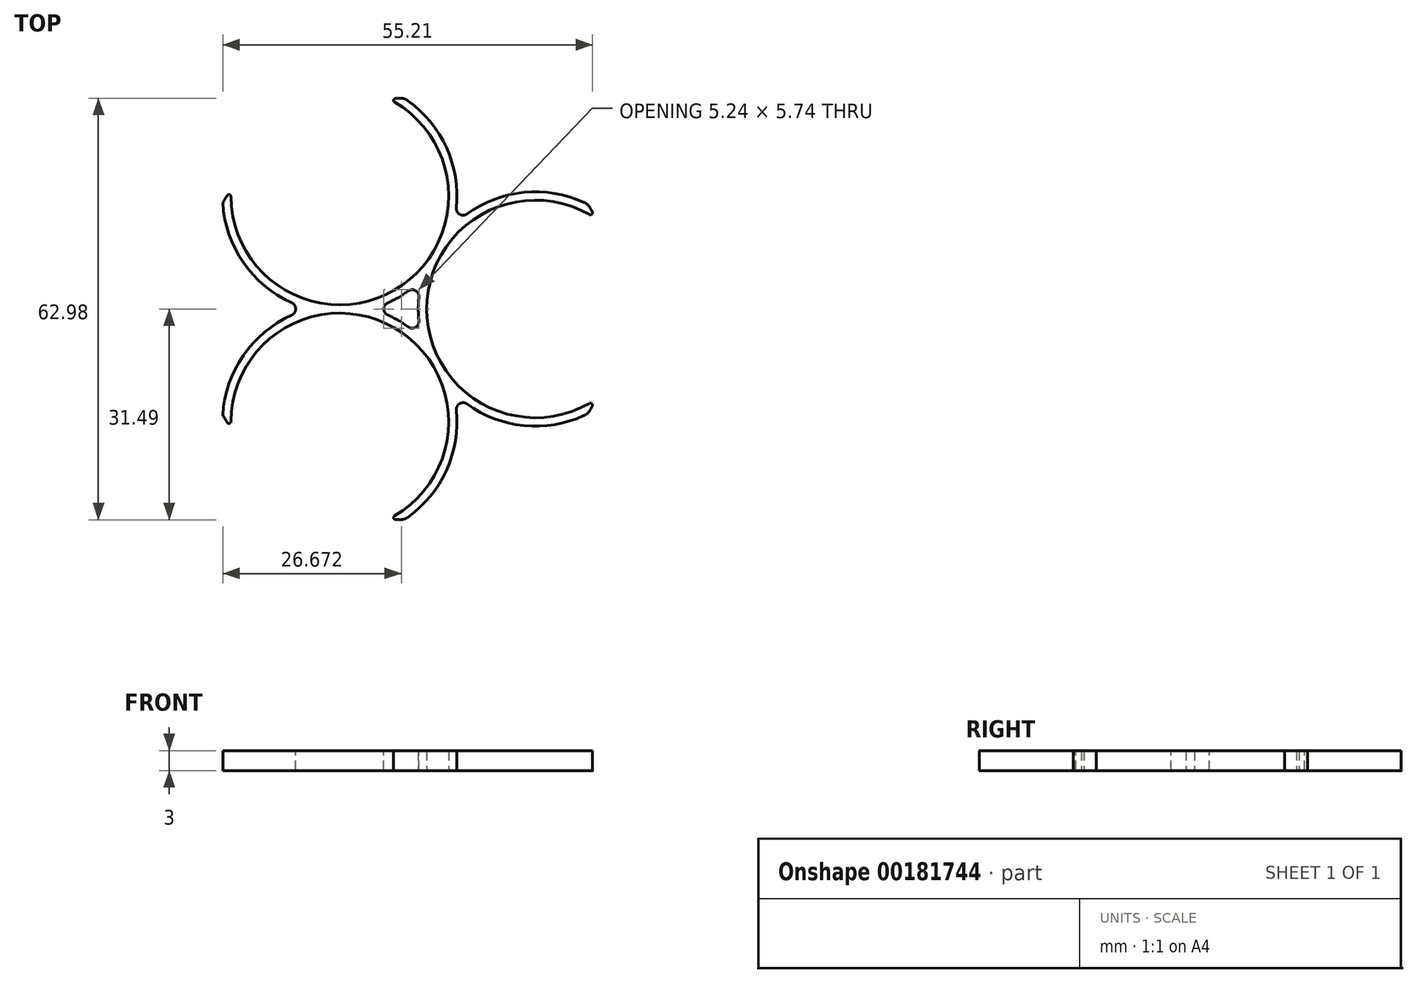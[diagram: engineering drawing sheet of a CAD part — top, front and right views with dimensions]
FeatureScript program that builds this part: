
annotation { "Feature Type Name" : "Feature", "Feature Type Description" : "" }
export const myFeature = defineFeature(function(context is Context, id is Id, definition is map)
    precondition{}
    {
        {
            var Q0;
            Q0=qCreatedBy(makeId("Top.planeOp"),FACE);
            var sketch = newSketch(context, id + "F0", { "sketchPlane" : qUnion([Q0])});
            skArc(sketch, "E0", {"start": v(-12.3, -12.45) * mm, "mid": v(-2.73, -17.29) * mm, "end": v(7.86, -15.64) * mm});
            skArc(sketch, "E1", {"start": v(8.94, 13.57) * mm, "mid": v(-16.25, 0) * mm, "end": v(8.94, -13.57) * mm});
            skArc(sketch, "E2.1.0", {"start": v(-46.7, 15.86) * mm, "mid": v(-42.83, 5.87) * mm, "end": v(-33.86, 0) * mm});
            skArc(sketch, "E2.1.1", {"start": v(-45.45, 17.84) * mm, "mid": v(-21.1, 2.8) * mm, "end": v(-21.95, 31.4) * mm});
            skArc(sketch, "E2.2.0", {"start": v(-19.62, -31.5) * mm, "mid": v(-12.9, -23.15) * mm, "end": v(-12.3, -12.45) * mm});
            skArc(sketch, "E2.2.1", {"start": v(-21.95, -31.4) * mm, "mid": v(-21.1, -2.8) * mm, "end": v(-45.45, -17.84) * mm});
            skPoint(sketch, "E2.center", {"position": v(-19.49, 0) * mm});
            skArc(sketch, "E3", {"start": v(-45.45, 17.84) * mm, "mid": v(-46.1, 16.86) * mm, "end": v(-46.7, 15.86) * mm});
            skArc(sketch, "E4.trimOffspring", {"start": v(-46.7, -15.86) * mm, "mid": v(-46.1, -16.86) * mm, "end": v(-45.45, -17.84) * mm});
            skArc(sketch, "E5.trimOffspring", {"start": v(-21.95, -31.4) * mm, "mid": v(-20.78, -31.47) * mm, "end": v(-19.62, -31.5) * mm});
            skArc(sketch, "E6.trimOffspring", {"start": v(7.86, -15.64) * mm, "mid": v(8.42, -14.61) * mm, "end": v(8.94, -13.57) * mm});
            skArc(sketch, "E7.trimOffspring", {"start": v(-16.93, -4.42) * mm, "mid": v(-20.48, -1.72) * mm, "end": v(-24.6, 0) * mm});
            skArc(sketch, "E8.trimOffspring", {"start": v(-12.3, 12.45) * mm, "mid": v(-12.9, 23.15) * mm, "end": v(-19.62, 31.5) * mm});
            skArc(sketch, "E9.trimOffspring", {"start": v(-16.93, 4.42) * mm, "mid": v(-17.5, 0) * mm, "end": v(-16.93, -4.42) * mm});
            skArc(sketch, "E10.trimOffspring", {"start": v(-33.86, 0) * mm, "mid": v(-42.83, -5.87) * mm, "end": v(-46.7, -15.86) * mm});
            skArc(sketch, "E11.trimOffspring", {"start": v(-24.6, 0) * mm, "mid": v(-20.48, 1.72) * mm, "end": v(-16.93, 4.42) * mm});
            skArc(sketch, "E12.trimOffspring", {"start": v(7.86, 15.64) * mm, "mid": v(-2.73, 17.29) * mm, "end": v(-12.3, 12.45) * mm});
            skArc(sketch, "E13.trimOffspring", {"start": v(8.94, 13.57) * mm, "mid": v(8.42, 14.61) * mm, "end": v(7.86, 15.64) * mm});
            skArc(sketch, "E14.trimOffspring", {"start": v(-19.62, 31.5) * mm, "mid": v(-20.78, 31.47) * mm, "end": v(-21.95, 31.4) * mm});
            skSolve(sketch);
        }
        {
            var Q0;
            Q0=makeQuery(id+"F0.imprint","IMPRINT",FACE,{"disambiguationData":[TD([[makeQuery(id+"F0.imprint","IMPRINT",EDGE,{"derivedFrom":sQuery(id+"F0.wireOp",EDGE,"E0")}),1.0]])]});
            extrude(context, id + "F1", {"entities" : qUnion([Q0]), "depth" : 3 * mm});
        }
        {
            var Q0;
            Q0=makeQuery(id+"F1.opExtrude","SWEPT_EDGE",EDGE,{"disambiguationData":[OSD([sQuery(id+"F0.wireOp",EDGE,"E2.1.0"),sQuery(id+"F0.wireOp",EDGE,"E10.trimOffspring")])]});
            var Q1;
            Q1=makeQuery(id+"F1.opExtrude","SWEPT_EDGE",EDGE,{"disambiguationData":[OSD([sQuery(id+"F0.wireOp",EDGE,"E8.trimOffspring"),sQuery(id+"F0.wireOp",EDGE,"E12.trimOffspring")])]});
            var Q2;
            Q2=makeQuery(id+"F1.opExtrude","SWEPT_EDGE",EDGE,{"disambiguationData":[OSD([sQuery(id+"F0.wireOp",EDGE,"E0"),sQuery(id+"F0.wireOp",EDGE,"E2.2.0")])]});
            fillet(context, id + "F2", {"entities" : qUnion([Q0, Q1, Q2]), "radius" : 1 * mm, "tangentPropagation" : true, "allowEdgeOverflow" : false});
        }
        {
            var Q0;
            Q0=makeQuery(id+"F1.opExtrude","SWEPT_EDGE",EDGE,{"disambiguationData":[OSD([sQuery(id+"F0.wireOp",EDGE,"E9.trimOffspring"),sQuery(id+"F0.wireOp",EDGE,"E11.trimOffspring")])]});
            var Q1;
            Q1=makeQuery(id+"F1.opExtrude","SWEPT_EDGE",EDGE,{"disambiguationData":[OSD([sQuery(id+"F0.wireOp",EDGE,"E7.trimOffspring"),sQuery(id+"F0.wireOp",EDGE,"E9.trimOffspring")])]});
            var Q2;
            Q2=makeQuery(id+"F1.opExtrude","SWEPT_EDGE",EDGE,{"disambiguationData":[OSD([sQuery(id+"F0.wireOp",EDGE,"E7.trimOffspring"),sQuery(id+"F0.wireOp",EDGE,"E11.trimOffspring")])]});
            fillet(context, id + "F3", {"entities" : qUnion([Q0, Q1, Q2]), "radius" : 1 * mm, "tangentPropagation" : true, "allowEdgeOverflow" : false});
        }
        {
            var Q0;
            Q0=makeQuery(id+"F1.opExtrude","SWEPT_EDGE",EDGE,{"disambiguationData":[OSD([sQuery(id+"F0.wireOp",EDGE,"E1"),sQuery(id+"F0.wireOp",EDGE,"E13.trimOffspring")])]});
            var Q1;
            Q1=makeQuery(id+"F1.opExtrude","SWEPT_EDGE",EDGE,{"disambiguationData":[OSD([sQuery(id+"F0.wireOp",EDGE,"E1"),sQuery(id+"F0.wireOp",EDGE,"E6.trimOffspring")])]});
            var Q2;
            Q2=makeQuery(id+"F1.opExtrude","SWEPT_EDGE",EDGE,{"disambiguationData":[OSD([sQuery(id+"F0.wireOp",EDGE,"E2.2.1"),sQuery(id+"F0.wireOp",EDGE,"E5.trimOffspring")])]});
            var Q3;
            Q3=makeQuery(id+"F1.opExtrude","SWEPT_EDGE",EDGE,{"disambiguationData":[OSD([sQuery(id+"F0.wireOp",EDGE,"E2.2.1"),sQuery(id+"F0.wireOp",EDGE,"E4.trimOffspring")])]});
            var Q4;
            Q4=makeQuery(id+"F1.opExtrude","SWEPT_EDGE",EDGE,{"disambiguationData":[OSD([sQuery(id+"F0.wireOp",EDGE,"E2.1.1"),sQuery(id+"F0.wireOp",EDGE,"E14.trimOffspring")])]});
            var Q5;
            Q5=makeQuery(id+"F1.opExtrude","SWEPT_EDGE",EDGE,{"disambiguationData":[OSD([sQuery(id+"F0.wireOp",EDGE,"E2.1.1"),sQuery(id+"F0.wireOp",EDGE,"E3")])]});
            fillet(context, id + "F4", {"entities" : qUnion([Q0, Q1, Q2, Q3, Q4, Q5]), "radius" : .3 * mm, "tangentPropagation" : true, "allowEdgeOverflow" : false});
        }
        {
            var Q0;
            Q0=makeQuery(id+"F1.opExtrude","SWEPT_EDGE",EDGE,{"disambiguationData":[OSD([sQuery(id+"F0.wireOp",EDGE,"E12.trimOffspring"),sQuery(id+"F0.wireOp",EDGE,"E13.trimOffspring")])]});
            var Q1;
            Q1=makeQuery(id+"F1.opExtrude","SWEPT_EDGE",EDGE,{"disambiguationData":[OSD([sQuery(id+"F0.wireOp",EDGE,"E8.trimOffspring"),sQuery(id+"F0.wireOp",EDGE,"E14.trimOffspring")])]});
            var Q2;
            Q2=makeQuery(id+"F1.opExtrude","SWEPT_EDGE",EDGE,{"disambiguationData":[OSD([sQuery(id+"F0.wireOp",EDGE,"E0"),sQuery(id+"F0.wireOp",EDGE,"E6.trimOffspring")])]});
            var Q3;
            Q3=makeQuery(id+"F1.opExtrude","SWEPT_EDGE",EDGE,{"disambiguationData":[OSD([sQuery(id+"F0.wireOp",EDGE,"E2.2.0"),sQuery(id+"F0.wireOp",EDGE,"E5.trimOffspring")])]});
            fillet(context, id + "F5", {"entities" : qUnion([Q0, Q1, Q2, Q3]), "radius" : 2 * mm, "tangentPropagation" : true, "allowEdgeOverflow" : false});
        }
    });
